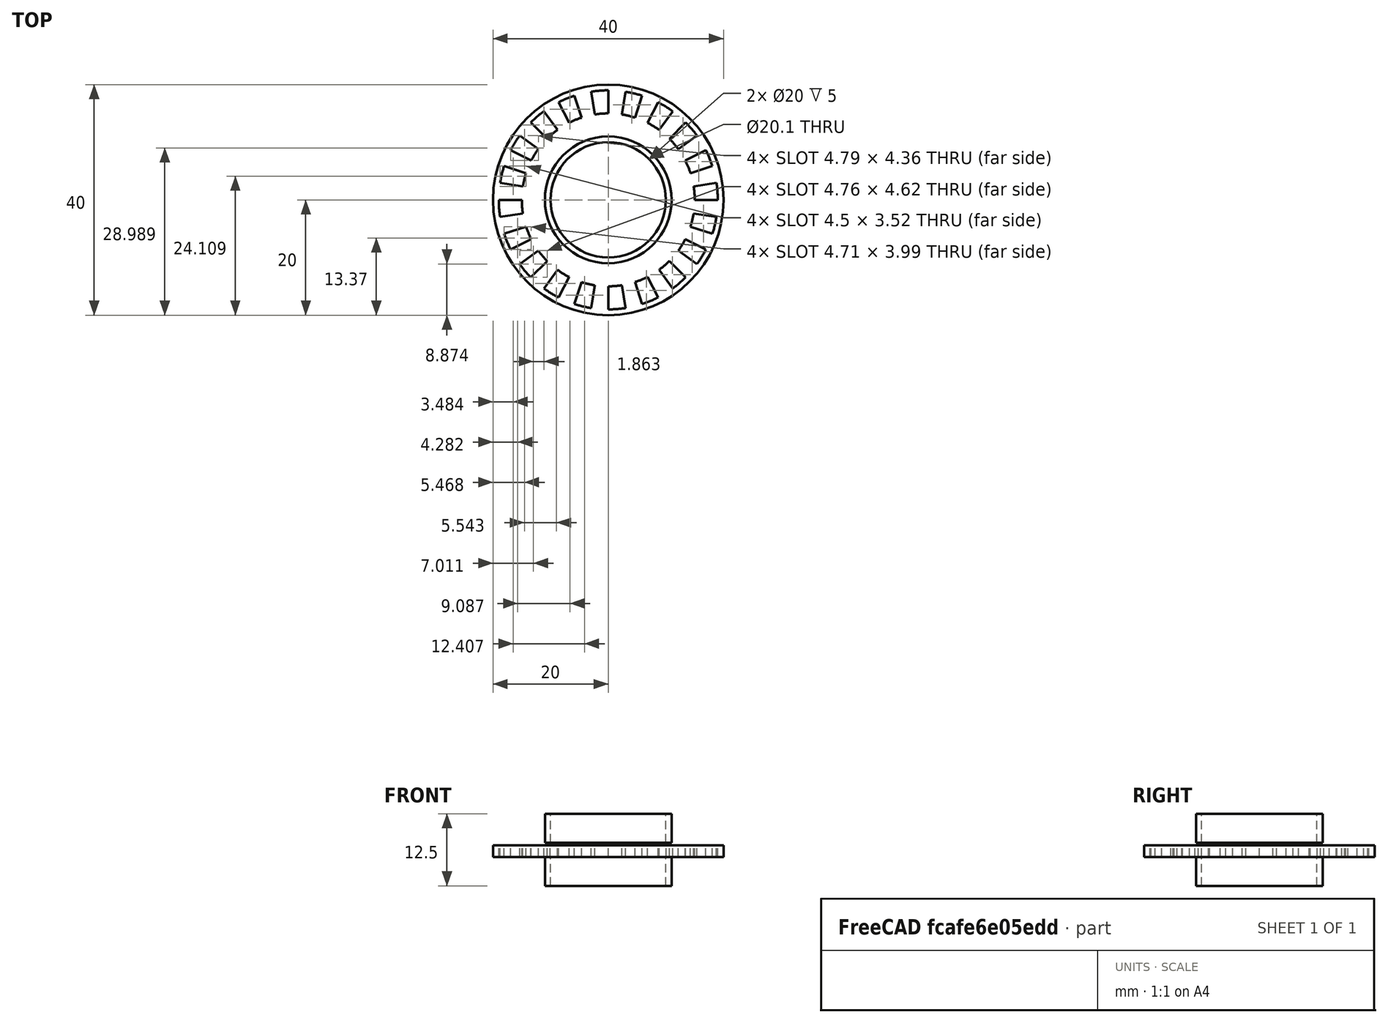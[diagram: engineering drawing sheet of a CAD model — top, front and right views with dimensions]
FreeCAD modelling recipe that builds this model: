
FCSTD DOCUMENT  (FreeCAD 0.18R16146 (Git))
Label: decoder_ring
License: All rights reserved
LicenseURL: http://en.wikipedia.org/wiki/All_rights_reserved
objects: Part::Extrusion×20, Part::Cylinder×6, Part::Cut×4, Part::Part2DObjectPython×4, Sketcher::SketchObject×2, Part::MultiFuse×1, App::DocumentObjectGroup×1
note: 37 computed .brp shape members not serialized (recipe doc carries the construction recipe); baked Part::Feature solids carry a one-line shape summary decoded from their .brp

FEATURE [Sketcher::SketchObject] Sketch001
  sketch-geometry (8):
    g0: ArcOfCircle CenterX=0 CenterY=0 CenterZ=0 NormalX=0 NormalY=0 NormalZ=1 AngleXU=0 Radius=19 StartAngle=0 EndAngle=0.15708
    g1: LineSegment StartX=19 StartY=0 StartZ=0 EndX=15 EndY=0 EndZ=0
    g2: LineSegment StartX=18.7661 StartY=2.97225 StartZ=0 EndX=14.8153 EndY=2.34652 EndZ=0
    g3: ArcOfCircle CenterX=0 CenterY=0 CenterZ=0 NormalX=0 NormalY=0 NormalZ=1 AngleXU=0 Radius=15 StartAngle=0 EndAngle=0.15708
    g4: GeomPoint X=14.8153 Y=2.34652 Z=0
    g5: GeomPoint X=15 Y=0 Z=0
    g6: GeomPoint X=19.0173 Y=-0.000551 Z=0
    g7: GeomPoint X=18.7661 Y=2.97226 Z=0
FEATURE [Part::Cylinder] Cylinder001  label="Zylinder001"
  Angle = 360
  AttacherType = Attacher::AttachEngine3D
  Height = 2
  Radius = 20
FEATURE [Part::Extrusion] Extrude010
  Base = -> Sketch001
  Dir = (0,0,1)
  DirMode = 2
  FaceMakerClass = Part::FaceMakerBullseye
  LengthFwd = 3
  LengthRev = 0
  Placement = pos=(0,0,0) rot=(0,0,1;3.14159rad)
  Solid = true
  Symmetric = false
FEATURE [Part::Extrusion] Extrude001
  Base = -> Sketch001
  Dir = (0,0,1)
  DirMode = 2
  FaceMakerClass = Part::FaceMakerBullseye
  LengthFwd = 3
  LengthRev = 0
  Placement = pos=(0,0,0) rot=(0,0,1;0.314159rad)
  Solid = true
  Symmetric = false
FEATURE [Part::Extrusion] Extrude014
  Base = -> Sketch001
  Dir = (0,0,1)
  DirMode = 2
  FaceMakerClass = Part::FaceMakerBullseye
  LengthFwd = 3
  LengthRev = 0
  Placement = pos=(0,0,0) rot=(0,0,-1;1.88496rad)
  Solid = true
  Symmetric = false
FEATURE [Part::Extrusion] Extrude016
  Base = -> Sketch001
  Dir = (0,0,1)
  DirMode = 2
  FaceMakerClass = Part::FaceMakerBullseye
  LengthFwd = 3
  LengthRev = 0
  Placement = pos=(0,0,0) rot=(0,0,-1;1.25664rad)
  Solid = true
  Symmetric = false
FEATURE [Part::Extrusion] Extrude017
  Base = -> Sketch001
  Dir = (0,0,1)
  DirMode = 2
  FaceMakerClass = Part::FaceMakerBullseye
  LengthFwd = 3
  LengthRev = 0
  Placement = pos=(0,0,0) rot=(0,0,-1;0.942478rad)
  Solid = true
  Symmetric = false
FEATURE [Part::Extrusion] Extrude003
  Base = -> Sketch001
  Dir = (0,0,1)
  DirMode = 2
  FaceMakerClass = Part::FaceMakerBullseye
  LengthFwd = 3
  LengthRev = 0
  Placement = pos=(0,0,0) rot=(0,0,1;0.942478rad)
  Solid = true
  Symmetric = false
FEATURE [Part::Extrusion] Extrude002
  Base = -> Sketch001
  Dir = (0,0,1)
  DirMode = 2
  FaceMakerClass = Part::FaceMakerBullseye
  LengthFwd = 3
  LengthRev = 0
  Placement = pos=(0,0,0) rot=(0,0,1;0.628319rad)
  Solid = true
  Symmetric = false
FEATURE [Part::Extrusion] Extrude013
  Base = -> Sketch001
  Dir = (0,0,1)
  DirMode = 2
  FaceMakerClass = Part::FaceMakerBullseye
  LengthFwd = 3
  LengthRev = 0
  Placement = pos=(0,0,0) rot=(0,0,1;4.08407rad)
  Solid = true
  Symmetric = false
FEATURE [Part::Extrusion] Extrude006
  Base = -> Sketch001
  Dir = (0,0,1)
  DirMode = 2
  FaceMakerClass = Part::FaceMakerBullseye
  LengthFwd = 3
  LengthRev = 0
  Placement = pos=(0,0,0) rot=(0,0,1;1.88496rad)
  Solid = true
  Symmetric = false
FEATURE [Part::Extrusion] Extrude012
  Base = -> Sketch001
  Dir = (0,0,1)
  DirMode = 2
  FaceMakerClass = Part::FaceMakerBullseye
  LengthFwd = 3
  LengthRev = 0
  Placement = pos=(0,0,0) rot=(0,0,1;3.76991rad)
  Solid = true
  Symmetric = false
FEATURE [Part::Extrusion] Extrude015
  Base = -> Sketch001
  Dir = (0,0,1)
  DirMode = 2
  FaceMakerClass = Part::FaceMakerBullseye
  LengthFwd = 3
  LengthRev = 0
  Placement = pos=(0,0,0) rot=(0,0,-1;1.5708rad)
  Solid = true
  Symmetric = false
FEATURE [Part::Extrusion] Extrude018
  Base = -> Sketch001
  Dir = (0,0,1)
  DirMode = 2
  FaceMakerClass = Part::FaceMakerBullseye
  LengthFwd = 3
  LengthRev = 0
  Placement = pos=(0,0,0) rot=(0,0,-1;0.628319rad)
  Solid = true
  Symmetric = false
FEATURE [Part::Extrusion] Extrude009
  Base = -> Sketch001
  Dir = (0,0,1)
  DirMode = 2
  FaceMakerClass = Part::FaceMakerBullseye
  LengthFwd = 3
  LengthRev = 0
  Placement = pos=(0,0,0) rot=(0,0,1;2.82743rad)
  Solid = true
  Symmetric = false
FEATURE [Part::Extrusion] Extrude005
  Base = -> Sketch001
  Dir = (0,0,1)
  DirMode = 2
  FaceMakerClass = Part::FaceMakerBullseye
  LengthFwd = 3
  LengthRev = 0
  Placement = pos=(0,0,0) rot=(0,0,1;1.5708rad)
  Solid = true
  Symmetric = false
FEATURE [Part::Extrusion] Extrude019
  Base = -> Sketch001
  Dir = (0,0,1)
  DirMode = 2
  FaceMakerClass = Part::FaceMakerBullseye
  LengthFwd = 3
  LengthRev = 0
  Placement = pos=(0,0,0) rot=(0,0,-1;0.314159rad)
  Solid = true
  Symmetric = false
FEATURE [Part::Extrusion] Extrude007
  Base = -> Sketch001
  Dir = (0,0,1)
  DirMode = 2
  FaceMakerClass = Part::FaceMakerBullseye
  LengthFwd = 3
  LengthRev = 0
  Placement = pos=(0,0,0) rot=(0,0,1;2.19911rad)
  Solid = true
  Symmetric = false
FEATURE [Part::Extrusion] Extrude004
  Base = -> Sketch001
  Dir = (0,0,1)
  DirMode = 2
  FaceMakerClass = Part::FaceMakerBullseye
  LengthFwd = 3
  LengthRev = 0
  Placement = pos=(0,0,0) rot=(0,0,1;1.25664rad)
  Solid = true
  Symmetric = false
FEATURE [Part::Extrusion] Extrude011
  Base = -> Sketch001
  Dir = (0,0,1)
  DirMode = 2
  FaceMakerClass = Part::FaceMakerBullseye
  LengthFwd = 3
  LengthRev = 0
  Placement = pos=(0,0,0) rot=(0,0,1;3.45575rad)
  Solid = true
  Symmetric = false
FEATURE [Part::Cylinder] Cylinder  label="Zylinder"
  Angle = 360
  AttacherType = Attacher::AttachEngine3D
  Height = 2
  Radius = 10.05
FEATURE [Part::Extrusion] Extrude
  Base = -> Sketch001
  Dir = (0,0,1)
  DirMode = 2
  FaceMakerClass = Part::FaceMakerBullseye
  LengthFwd = 3
  LengthRev = 0
  Solid = true
  Symmetric = false
FEATURE [Part::Extrusion] Extrude008
  Base = -> Sketch001
  Dir = (0,0,1)
  DirMode = 2
  FaceMakerClass = Part::FaceMakerBullseye
  LengthFwd = 3
  LengthRev = 0
  Placement = pos=(0,0,0) rot=(0,0,1;2.51327rad)
  Solid = true
  Symmetric = false
FEATURE [Part::Cut] Cut
  Base = -> Cylinder001
  Tool = -> Cylinder
FEATURE [Part::Cylinder] Cylinder003  label="Zylinder003"
  Angle = 360
  AttacherType = Attacher::AttachEngine3D
  Height = 5
  Placement = pos=(40,0,0) rot=(0,0,1;0rad)
  Radius = 11
FEATURE [Part::MultiFuse] Fusion
  Shapes = -> [Extrude001,Extrude011,Extrude012,Extrude005,Extrude007,Extrude008,Extrude006,Extrude003,Extrude004,Extrude002,Extrude010,Extrude009,Extrude016,Extrude019,Extrude018,Extrude015,Extrude017,Extrude014,Extrude013,Extrude]
FEATURE [Part::Cylinder] Cylinder002  label="Zylinder002"
  Angle = 360
  AttacherType = Attacher::AttachEngine3D
  Height = 5
  Placement = pos=(40,0,0) rot=(0,0,1;0rad)
  Radius = 10
FEATURE [Part::Cylinder] Cylinder004  label="Zylinder004"
  Angle = 360
  AttacherType = Attacher::AttachEngine3D
  Height = 5
  Placement = pos=(40,0,0) rot=(0,0,1;0rad)
  Radius = 10
FEATURE [Part::Cylinder] Cylinder005  label="Zylinder005"
  Angle = 360
  AttacherType = Attacher::AttachEngine3D
  Height = 5
  Placement = pos=(40,0,0) rot=(0,0,1;0rad)
  Radius = 11
FEATURE [Part::Part2DObjectPython] Arc  # Draft 2D object (typed FeaturePython)
  FirstAngle = 0
  LastAngle = 9
  MakeFace = true
  Radius = 19
FEATURE [Part::Part2DObjectPython] Arc002  # Draft 2D object (typed FeaturePython)
  FirstAngle = 0
  LastAngle = 9
  MakeFace = true
  Radius = 15
FEATURE [Part::Part2DObjectPython] Line  # Draft 2D object (typed FeaturePython)
  ChamferSize = 0
  Closed = false
  End = (15,0,0)
  FilletRadius = 0
  Length = 4
  MakeFace = true
  Points = (2) [(19,5.51091e-16,0),(15,-3.67394e-17,0)]
  Start = (19,0,0)
  Subdivisions = 0
FEATURE [Part::Part2DObjectPython] Line001  # Draft 2D object (typed FeaturePython)
  ChamferSize = 0
  Closed = false
  End = (14.8153,2.34652,0)
  FilletRadius = 0
  Length = 4
  MakeFace = true
  Placement = pos=(0,0,0) rot=(0,0,1;0.15708rad)
  Points = (2) [(19,-4.44089e-16,0),(15,-4.44089e-16,0)]
  Start = (18.7661,2.97225,0)
  Subdivisions = 0
FEATURE [App::DocumentObjectGroup] Gruppe001
  Group = -> [Arc,Arc002,Line,Line001]
FEATURE [Sketcher::SketchObject] Sketch
  sketch-geometry (5):
    g0: ArcOfCircle CenterX=0 CenterY=0 CenterZ=0 NormalX=0 NormalY=0 NormalZ=1 AngleXU=0 Radius=18 StartAngle=0 EndAngle=0.15708
    g1: ArcOfCircle CenterX=0 CenterY=0 CenterZ=0 NormalX=0 NormalY=0 NormalZ=1 AngleXU=0 Radius=15 StartAngle=0 EndAngle=0.15708
    g2: LineSegment StartX=18 StartY=0 StartZ=0 EndX=15 EndY=0 EndZ=0
    g3: LineSegment StartX=17.7784 StartY=2.81582 StartZ=0 EndX=14.8153 EndY=2.34652 EndZ=0
    g4: ArcOfCircle CenterX=0.017415 CenterY=-0.013502 CenterZ=0 NormalX=0 NormalY=0 NormalZ=1 AngleXU=0 Radius=19.0333 StartAngle=6.28316 EndAngle=6.44
FEATURE [Part::Cut] Cut001
  Base = -> Cut
  Tool = -> Fusion
FEATURE [Part::Cut] Cut003
  Base = -> Cylinder005
  Placement = pos=(-40,0,2.5) rot=(0,0,1;0rad)
  Tool = -> Cylinder004
FEATURE [Part::Cut] Cut002
  Base = -> Cylinder003
  Placement = pos=(-40,0,-5) rot=(0,0,1;0rad)
  Tool = -> Cylinder002
